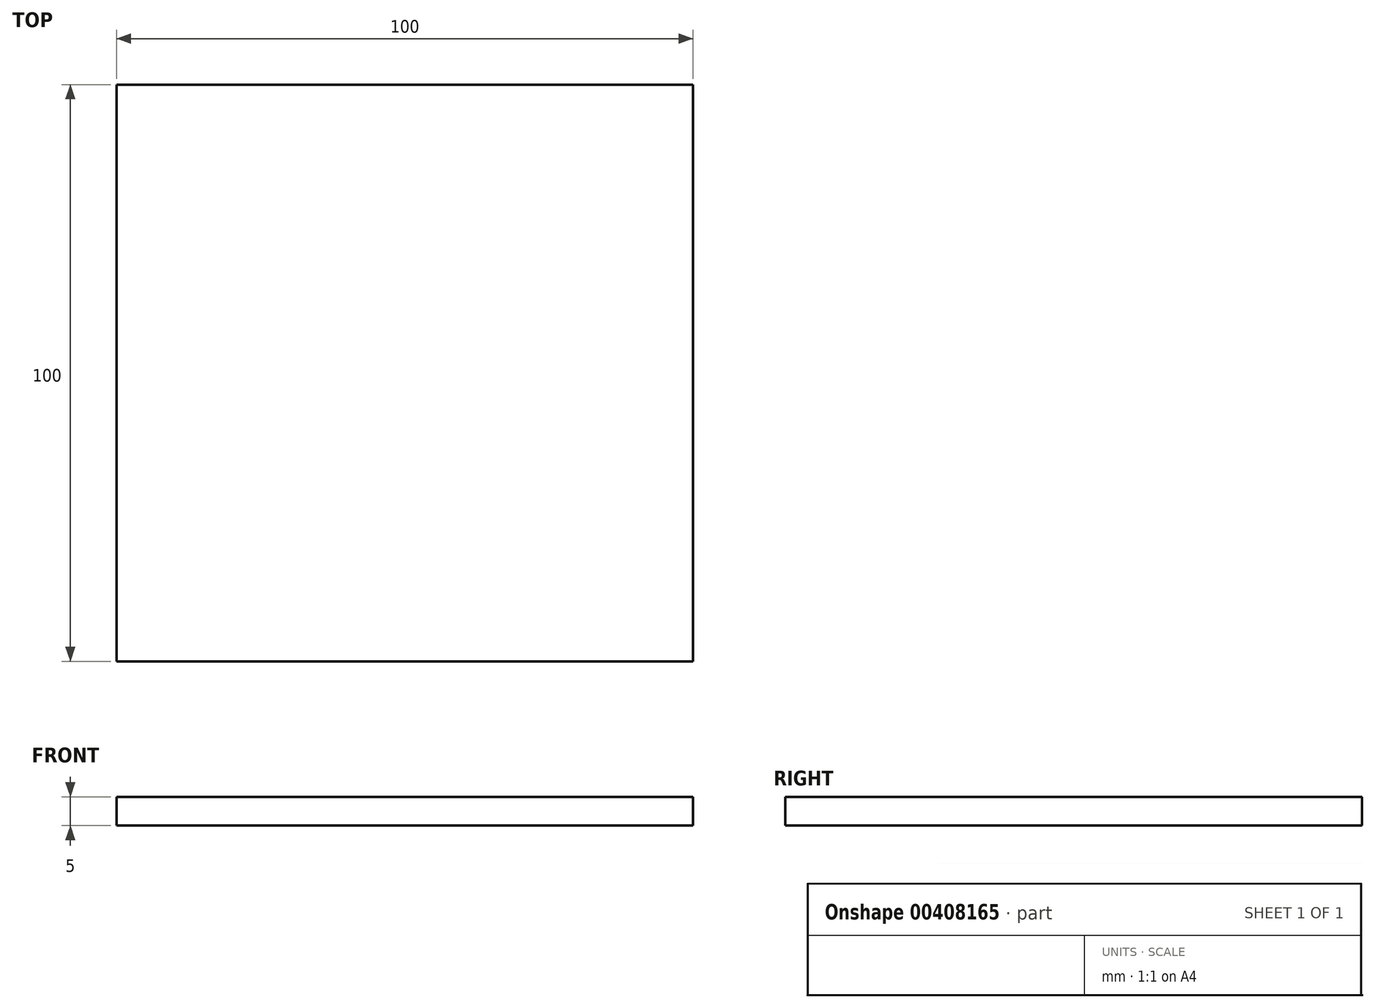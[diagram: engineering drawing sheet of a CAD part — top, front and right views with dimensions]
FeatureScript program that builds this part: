
annotation { "Feature Type Name" : "Feature", "Feature Type Description" : "" }
export const myFeature = defineFeature(function(context is Context, id is Id, definition is map)
    precondition{}
    {
        {
            var Q0;
            Q0=qCreatedBy(makeId("Top.planeOp"),FACE);
            var sketch = newSketch(context, id + "F0", { "sketchPlane" : qUnion([Q0])});
            skLineSegment(sketch, "E0.bottom", {"start": v(0, 0) * mm, "end": v(100, 0) * mm});
            skLineSegment(sketch, "E0.top", {"start": v(0, -100) * mm, "end": v(100, -100) * mm});
            skLineSegment(sketch, "E0.left", {"start": v(0, 0) * mm, "end": v(0, -100) * mm});
            skLineSegment(sketch, "E0.right", {"start": v(100, 0) * mm, "end": v(100, -100) * mm});
            skSolve(sketch);
        }
        {
            var Q0;
            Q0 = qSketchRegion(id + "F0", true);
            extrude(context, id + "F1", {"entities" : qUnion([Q0]), "depth" : 5 * mm});
        }
    });
